# Revit family: Bticino Portiers IP - Poste de gardiennage
name_source: partatom
category: Equipement électrique
units: mm (PartAtom-declared; Revit-internal decimal feet)

## family parameters
Basée sur le plan de construction = Non
Configuration du panneau = Deux colonnes, circuits au sein
Cote de connecteur circulaire = Utiliser le diamètre
Couper avec des vides une fois chargée = Non
Partagée = Non
Point de calcul de pièce = Non
Toujours verticalement = Oui
Type d'élément = Tableau de raccordement

## types (1)
- IP - CENTRALE DE CONCIERGERIE
    Conditions Générale d'Utilisation = https://export.legrand.com
    Désignation produit = IP - CENTRALE DE CONCIERGERIE
    Ecran Tactile = Oui
    Elévation par défaut = 0 mm  [stored 0 ft]
    Fabricant = BTICINO
    Hauteur = 211 mm
    IP = 30
    Largeur = 308 mm
    Mode de pose = Appareil de table
    Profondeur = 170 mm  [stored 0.557743 ft]
    Référence / Modèle = BT-375000
    Site web configurateur = https://www.homesystems-legrandgroup.com
    Temperature d'utilisation MIN-MAX = -10/+55 °C
    Tension = 24 V DC
    Type d'interface = Full-duplex
    Type de raccordement = Réseau

note: [stored X ft] marks values corroborated as IEEE doubles in the binary element streams (Revit-internal decimal feet)
